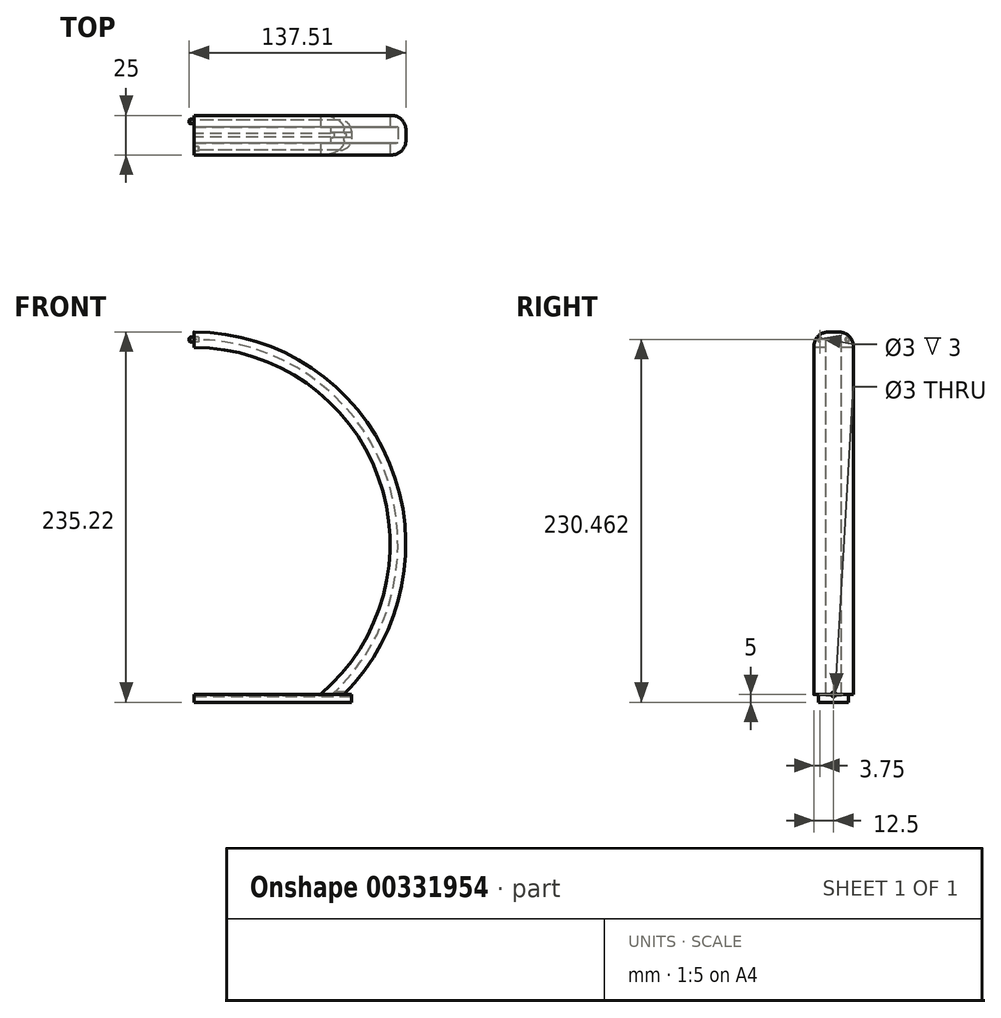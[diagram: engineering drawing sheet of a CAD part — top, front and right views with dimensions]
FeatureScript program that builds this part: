
annotation { "Feature Type Name" : "Feature", "Feature Type Description" : "" }
export const myFeature = defineFeature(function(context is Context, id is Id, definition is map)
    precondition{}
    {
        {
            var Q0;
            Q0=qCreatedBy(makeId("Front.planeOp"),FACE);
            var sketch = newSketch(context, id + "F0", { "sketchPlane" : qUnion([Q0])});
            skLineSegment(sketch, "E0", {"start": v(-96.18, 0) * mm, "end": v(95.2, 0) * mm});
            skArc(sketch, "E1", {"start": v(95.2, 0) * mm, "mid": v(-0.49, 230.22) * mm, "end": v(-96.18, 0) * mm});
            skSolve(sketch);
        }
        {
            var Q0;
            Q0=qSketchRegion(id+"F0",true);
            extrude(context, id + "F1", {"entities" : qUnion([Q0]), "endBound" : BoundingType.SYMMETRIC, "depth" : 25 * mm, "offsetDistance" : 25 * mm});
        }
        {
            var Q0;
            Q0=makeQuery(id+"F1.opExtrude","CAP_FACE",FACE,{"disambiguationData":[OSD([sQuery(id+"F0.wireOp",EDGE,"E0"),sQuery(id+"F0.wireOp",EDGE,"E1")])],"isStart":false});
            var sketch = newSketch(context, id + "F2", { "sketchPlane" : qUnion([Q0])});
            skLineSegment(sketch, "E2", {"start": v(-96.18, 0) * mm, "end": v(-81.18, 0) * mm});
            skLineSegment(sketch, "E3", {"start": v(95.2, 0) * mm, "end": v(80.2, 0) * mm});
            skArc(sketch, "E4", {"start": v(80.2, 0) * mm, "mid": v(-0.49, 220.46) * mm, "end": v(-81.18, 0) * mm});
            skSolve(sketch);
        }
        {
            var Q0;
            {var subQ0=sQuery(id+"F2.wireOp",EDGE,"E4");Q0=makeQuery(id+"F2.imprint","IMPRINT",FACE,{"disambiguationData":[TD([[makeQuery(id+"F2.imprint","IMPRINT",EDGE,{"derivedFrom":subQ0}),1.0]])]});}
            extrude(context, id + "F3", {"entities" : qUnion([Q0]), "operationType" : NewBodyOperationType.REMOVE, "endBound" : BoundingType.SYMMETRIC, "oppositeDirection" : true, "depth" : 290 * mm, "offsetDistance" : 25 * mm});
        }
        {
            var Q0;
            Q0=qCreatedBy(makeId("Top.planeOp"),FACE);
            var sketch = newSketch(context, id + "F4", { "sketchPlane" : qUnion([Q0])});
            skLineSegment(sketch, "E5.bottom", {"start": v(100, 9.5) * mm, "end": v(-100, 9.5) * mm});
            skLineSegment(sketch, "E5.top", {"start": v(100, -9.5) * mm, "end": v(-100, -9.5) * mm});
            skLineSegment(sketch, "E5.left", {"start": v(100, 9.5) * mm, "end": v(100, -9.5) * mm});
            skLineSegment(sketch, "E5.right", {"start": v(-100, 9.5) * mm, "end": v(-100, -9.5) * mm});
            skPoint(sketch, "E5.middle", {"position": v(0, 0) * mm});
            skSolve(sketch);
        }
        {
            var Q0;
            Q0=qSketchRegion(id+"F4",true);
            extrude(context, id + "F5", {"entities" : qUnion([Q0]), "operationType" : NewBodyOperationType.ADD, "oppositeDirection" : true, "depth" : 5 * mm, "offsetDistance" : 25 * mm});
        }
        {
            var Q0;
            Q0=qCreatedBy(makeId("Front.planeOp"),FACE);
            var sketch = newSketch(context, id + "F6", { "sketchPlane" : qUnion([Q0])});
            skLineSegment(sketch, "E6", {"start": v(-87.56, -1.07) * mm, "end": v(86.58, -1.07) * mm});
            skArc(sketch, "E7.0", {"start": v(86.58, -1.07) * mm, "mid": v(-0.49, 225.46) * mm, "end": v(-87.56, -1.07) * mm});
            skSolve(sketch);
        }
        {
            var Q0;
            Q0=qSketchRegion(id+"F6",true);
            extrude(context, id + "F7", {"entities" : qUnion([Q0]), "operationType" : NewBodyOperationType.REMOVE, "endBound" : BoundingType.SYMMETRIC, "oppositeDirection" : true, "depth" : 10 * mm});
        }
        {
            var Q0;
            Q0=qCreatedBy(makeId("Right.planeOp"),FACE);
            var sketch = newSketch(context, id + "F8", { "sketchPlane" : qUnion([Q0])});
            skCircle(sketch, "E8", {"center": v(0, 0) * mm, "radius": 1 * mm});
            skSolve(sketch);
        }
        {
            var Q0;
            Q0=qSketchRegion(id+"F8",true);
            extrude(context, id + "F9", {"entities" : qUnion([Q0]), "operationType" : NewBodyOperationType.REMOVE, "endBound" : BoundingType.THROUGH_ALL, "oppositeDirection" : true, "depth" : 25 * mm});
        }
        {
            var Q0;
            Q0=makeQuery(id+"F5.opExtrude","CAP_FACE",FACE,{"disambiguationData":[OSD([sQuery(id+"F4.wireOp",EDGE,"E5.bottom"),sQuery(id+"F4.wireOp",EDGE,"E5.top"),sQuery(id+"F4.wireOp",EDGE,"E5.left"),sQuery(id+"F4.wireOp",EDGE,"E5.right")])],"isStart":false});
            var sketch = newSketch(context, id + "F10", { "sketchPlane" : qUnion([Q0])});
            skLineSegment(sketch, "E9", {"start": v(0, 0) * mm, "end": v(43.09, 0) * mm});
            skLineSegment(sketch, "E10", {"start": v(0, 0) * mm, "end": v(-27.56, 0) * mm});
            skCircle(sketch, "E11", {"center": v(-27.56, 0) * mm, "radius": 2.5 * mm});
            skCircle(sketch, "E12", {"center": v(43.09, 0) * mm, "radius": 2.5 * mm});
            skSolve(sketch);
        }
        {
            var Q0;
            Q0=makeQuery(id+"F1.opExtrude","CAP_EDGE",EDGE,{"disambiguationData":[OSD([sQuery(id+"F0.wireOp",EDGE,"E1")])],"isStart":false});
            var Q1;
            Q1=makeQuery(id+"F1.opExtrude","CAP_EDGE",EDGE,{"disambiguationData":[OSD([sQuery(id+"F0.wireOp",EDGE,"E1")])],"isStart":true});
            fillet(context, id + "F11", {"entities" : qUnion([Q0, Q1]), "radius" : 9 * mm, "tangentPropagation" : true, "allowEdgeOverflow" : false});
        }
        {
            var Q0;
            Q0=qCreatedBy(makeId("Front.planeOp"),FACE);
            var sketch = newSketch(context, id + "F12", { "sketchPlane" : qUnion([Q0])});
            skLineSegment(sketch, "E13.bottom", {"start": v(0, -27.8) * mm, "end": v(-164.37, -27.8) * mm});
            skLineSegment(sketch, "E13.top", {"start": v(0, 271.3) * mm, "end": v(-164.37, 271.3) * mm});
            skLineSegment(sketch, "E13.left", {"start": v(0, -27.8) * mm, "end": v(0, 271.3) * mm});
            skLineSegment(sketch, "E13.right", {"start": v(-164.37, -27.8) * mm, "end": v(-164.37, 271.3) * mm});
            skSolve(sketch);
        }
        {
            var Q0;
            Q0 = qSketchRegion(id + "F12", true);
            extrude(context, id + "F13", {"entities" : qUnion([Q0]), "operationType" : NewBodyOperationType.REMOVE, "endBound" : BoundingType.SYMMETRIC, "oppositeDirection" : true, "depth" : 30 * mm});
        }
        {
            var Q0;
            {var subQ2=sQuery(id+"F0.wireOp",EDGE,"E1");Q0=makeQuery(id+"F13.boolean.opBoolean","COPY",FACE,{"disambiguationData":[TD([makeQuery(id+"F1.opExtrude","SWEPT_FACE",FACE,{"disambiguationData":[OSD([subQ2])]})])],"derivedFrom":makeQuery(id+"F13.opExtrude","SWEPT_FACE",FACE,{"disambiguationData":[OSD([sQuery(id+"F12.wireOp",EDGE,"E13.left")])]})});}
            var sketch = newSketch(context, id + "F14", { "sketchPlane" : qUnion([Q0])});
            skCircle(sketch, "E14", {"center": v(-8.75, 225.46) * mm, "radius": 1.5 * mm});
            skPoint(sketch, "E14.centerSnap0", {"position": v(-8.75, 220.46) * mm});
            skPoint(sketch, "E15.centerSnap0", {"position": v(8.75, 220.46) * mm});
            skSolve(sketch);
        }
        {
            var Q0;
            Q0=makeQuery(id+"F14.imprint","IMPRINT",FACE,{"disambiguationData":[TD([[makeQuery(id+"F14.imprint","IMPRINT",EDGE,{"derivedFrom":sQuery(id+"F14.wireOp",EDGE,"E14")}),1.0]])]});
            extrude(context, id + "F15", {"entities" : qUnion([Q0]), "operationType" : NewBodyOperationType.ADD, "depth" : 3 * mm});
        }
        {
            var Q0;
            {var subQ2=sQuery(id+"F0.wireOp",EDGE,"E1");Q0=makeQuery(id+"F13.boolean.opBoolean","COPY",FACE,{"disambiguationData":[TD([makeQuery(id+"F1.opExtrude","SWEPT_FACE",FACE,{"disambiguationData":[OSD([subQ2])]})])],"derivedFrom":makeQuery(id+"F13.opExtrude","SWEPT_FACE",FACE,{"disambiguationData":[OSD([sQuery(id+"F12.wireOp",EDGE,"E13.left")])]})});}
            var sketch = newSketch(context, id + "F16", { "sketchPlane" : qUnion([Q0])});
            skCircle(sketch, "E16", {"center": v(8.75, 225.46) * mm, "radius": 1.5 * mm});
            skPoint(sketch, "E16.centerSnap0", {"position": v(8.75, 220.46) * mm});
            skSolve(sketch);
        }
        {
            var Q0;
            Q0 = qSketchRegion(id + "F16", true);
            extrude(context, id + "F17", {"entities" : qUnion([Q0]), "operationType" : NewBodyOperationType.REMOVE, "oppositeDirection" : true, "depth" : 3 * mm});
        }
        {
            var Q0;
            Q0=makeQuery(id+"F15.opExtrude","CAP_EDGE",EDGE,{"disambiguationData":[OSD([sQuery(id+"F14.wireOp",EDGE,"E14")])],"isStart":false});
            chamfer(context, id + "F18", {"entities" : qUnion([Q0]), "width" : 0.5 * mm, "tangentPropagation" : true});
        }
        {
            var Q0;
            Q0=qCreatedBy(makeId("Right.planeOp"),FACE);
            var sketch = newSketch(context, id + "F19", { "sketchPlane" : qUnion([Q0])});
            skCircle(sketch, "E17", {"center": v(0, 0) * mm, "radius": 1.5 * mm});
            skSolve(sketch);
        }
        {
            var Q0;
            Q0 = qSketchRegion(id + "F19", true);
            extrude(context, id + "F20", {"entities" : qUnion([Q0]), "operationType" : NewBodyOperationType.REMOVE, "endBound" : BoundingType.THROUGH_ALL, "depth" : 25 * mm});
        }
        {
            var Q0;
            Q0=makeQuery(id+"F5.opExtrude","SWEPT_EDGE",EDGE,{"disambiguationData":[OSD([sQuery(id+"F4.wireOp",EDGE,"E5.bottom"),sQuery(id+"F4.wireOp",EDGE,"E5.left")])]});
            var Q1;
            Q1=makeQuery(id+"F5.opExtrude","SWEPT_EDGE",EDGE,{"disambiguationData":[OSD([sQuery(id+"F4.wireOp",EDGE,"E5.top"),sQuery(id+"F4.wireOp",EDGE,"E5.left")])]});
            fillet(context, id + "F21", {"entities" : qUnion([Q0, Q1]), "radius" : 7 * mm, "tangentPropagation" : true, "allowEdgeOverflow" : false});
        }
    });
